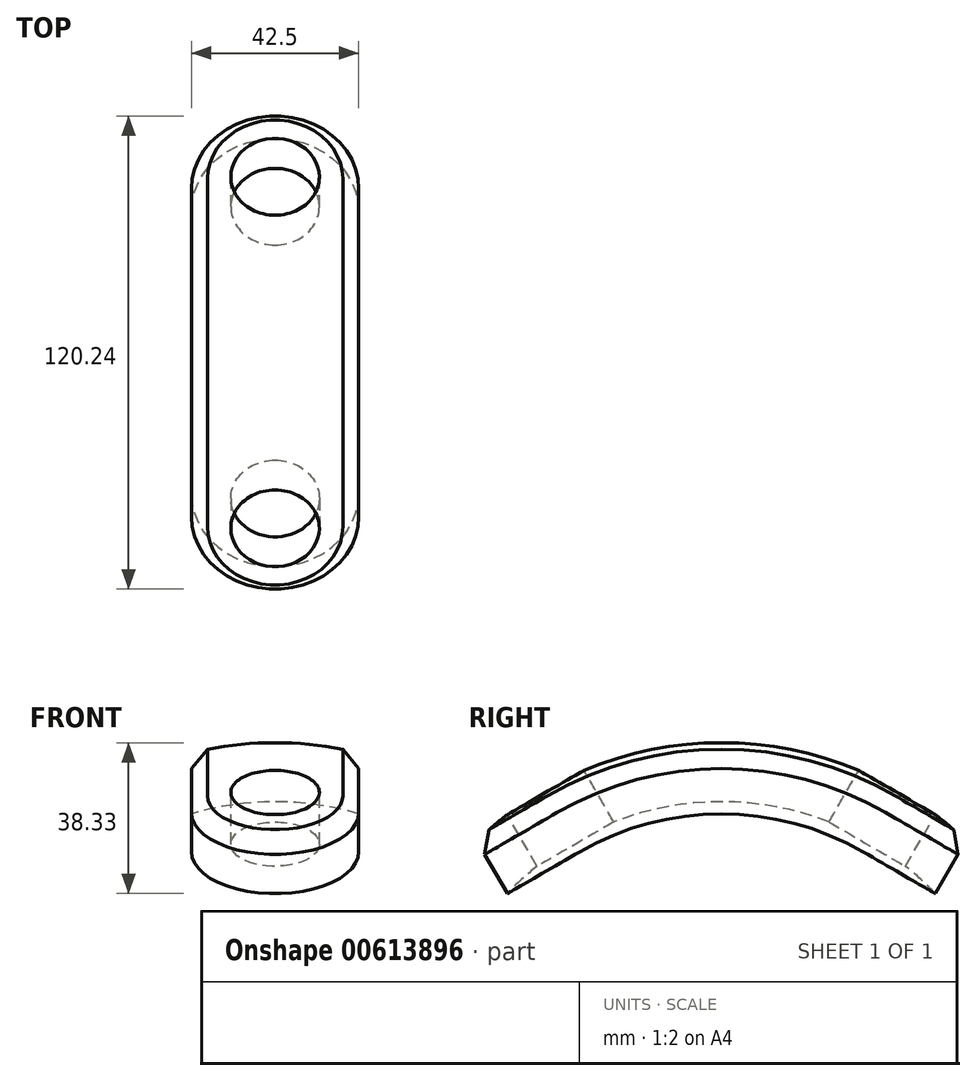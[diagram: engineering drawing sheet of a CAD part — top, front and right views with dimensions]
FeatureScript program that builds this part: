
annotation { "Feature Type Name" : "Feature", "Feature Type Description" : "" }
export const myFeature = defineFeature(function(context is Context, id is Id, definition is map)
    precondition{}
    {
        {
            var Q0;
            Q0=qCreatedBy(makeId("Front.planeOp"),FACE);
            var sketch = newSketch(context, id + "F0", { "sketchPlane" : qUnion([Q0])});
            skArc(sketch, "E0", {"start": v(21.25, 71.93) * mm, "mid": v(0, 75) * mm, "end": v(-21.25, 71.93) * mm});
            skArc(sketch, "E1", {"start": v(21.25, 87.46) * mm, "mid": v(0, 90) * mm, "end": v(-21.25, 87.46) * mm});
            skLineSegment(sketch, "E2", {"start": v(21.25, 71.93) * mm, "end": v(21.25, 87.46) * mm});
            skLineSegment(sketch, "E3.MirrorCS", {"start": v(-21.25, 71.93) * mm, "end": v(-21.25, 87.46) * mm});
            skLineSegment(sketch, "E4", {"start": v(0, 0) * mm, "end": v(12.01, 0) * mm, "construction": true});
            skSolve(sketch);
        }
        {
            var Q0;
            Q0=makeQuery(id+"F0.imprint","IMPRINT",FACE,{"disambiguationData":[TD([[makeQuery(id+"F0.imprint","IMPRINT",EDGE,{"derivedFrom":sQuery(id+"F0.wireOp",EDGE,"E0")}),-1.0]])]});
            var Q1;
            Q1=sQuery(id+"F0.wireOp",EDGE,"E4");
            revolve(context, id + "F1", {"entities" : qUnion([Q0]), "axis" : qUnion([Q1]), "revolveType" : RevolveType.ONE_DIRECTION, "angle" : 30 * degree});
        }
        {
            var Q0;
            Q0=makeQuery(id+"F1.opRevolve","CAP_EDGE",EDGE,{"disambiguationData":[OSD([sQuery(id+"F0.wireOp",EDGE,"E0")])],"isStart":false});
            cPoint(context, id + "F2", {"entities" : qUnion([Q0]), "parameter" : 0.5});
        }
        {
            var Q0;
            Q0=makeQuery(id+"F1.opRevolve","CAP_EDGE",EDGE,{"disambiguationData":[OSD([sQuery(id+"F0.wireOp",EDGE,"E2")])],"isStart":false});
            var Q1;
            Q1 = qCreatedBy(id + "F2" ,VERTEX);
            cPlane(context, id + "F3", {"entities" : qUnion([Q0, Q1]), "cplaneType" : CPlaneType.LINE_POINT, "offset" : 25 * mm, "width" : 150 * mm, "height" : 150 * mm});
        }
        {
            var Q0;
            Q0=qCreatedBy(id+"F3.planeOp",FACE);
            var sketch = newSketch(context, id + "F4", { "sketchPlane" : qUnion([Q0])});
            skCircle(sketch, "E5", {"center": v(0, 0) * mm, "radius": 11.25 * mm});
            skCircle(sketch, "E6", {"center": v(0, 0) * mm, "radius": 21.25 * mm});
            skLineSegment(sketch, "E7", {"start": v(11.25, 0) * mm, "end": v(21.25, 0) * mm});
            skLineSegment(sketch, "E8", {"start": v(-11.25, 0) * mm, "end": v(-21.25, 0) * mm});
            skLineSegment(sketch, "E9", {"start": v(-11.25, 0) * mm, "end": v(11.25, 0) * mm});
            skSolve(sketch);
        }
        {
            var Q0;
            {var subQ0=sQuery(id+"F4.wireOp",EDGE,"E9");Q0=makeQuery(id+"F4.imprint","IMPRINT",FACE,{"disambiguationData":[TD([[makeQuery(id+"F4.imprint","IMPRINT",EDGE,{"derivedFrom":subQ0}),-1.0]])]});}
            var Q1;
            {var subQ0=sQuery(id+"F4.wireOp",EDGE,"E9");Q1=makeQuery(id+"F4.imprint","IMPRINT",FACE,{"disambiguationData":[TD([[makeQuery(id+"F4.imprint","IMPRINT",EDGE,{"derivedFrom":subQ0}),1.0]])]});}
            extrude(context, id + "F5", {"entities" : qUnion([Q0, Q1]), "operationType" : NewBodyOperationType.REMOVE, "endBound" : BoundingType.THROUGH_ALL, "oppositeDirection" : true, "depth" : 25 * mm, "offsetDistance" : 25 * mm, "hasSecondDirection" : true, "secondDirectionBound" : SecondDirectionBoundingType.THROUGH_ALL, "secondDirectionOppositeDirection" : false, "secondDirectionDepth" : 25 * mm});
        }
        {
            var Q0;
            {var subQ0=sQuery(id+"F0.wireOp",EDGE,"E0");var subQ1=sQuery(id+"F0.wireOp",EDGE,"E1");var subQ2=sQuery(id+"F0.wireOp",EDGE,"E2");Q0=makeQuery(id+"F5.boolean.opBoolean","SPLIT",FACE,{"disambiguationData":[TD([makeQuery(id+"F1.opRevolve","SWEPT_FACE",FACE,{"disambiguationData":[OSD([subQ2])]})])],"derivedFrom":makeQuery(id+"F1.opRevolve","CAP_FACE",FACE,{"disambiguationData":[OSD([subQ0,subQ1,subQ2,sQuery(id+"F0.wireOp",EDGE,"E3.MirrorCS")])],"isStart":false})});}
            var Q1;
            Q1=makeQuery(id+"F5.boolean.opBoolean","COPY",FACE,{"derivedFrom":makeQuery(id+"F5.opExtrude","SWEPT_FACE",FACE,{"disambiguationData":[OSD([sQuery(id+"F4.wireOp",EDGE,"E5")])]})});
            revolve(context, id + "F6", {"operationType" : NewBodyOperationType.ADD, "entities" : qUnion([Q0]), "axis" : qUnion([Q1]), "revolveType" : RevolveType.ONE_DIRECTION, "angle" : 180 * degree});
        }
        {
            var Q0;
            Q0=makeQuery(id+"F1.opRevolve","SWEPT_BODY",BODY,{"disambiguationData":[OSD([sQuery(id+"F0.wireOp",EDGE,"E0"),sQuery(id+"F0.wireOp",EDGE,"E1"),sQuery(id+"F0.wireOp",EDGE,"E2"),sQuery(id+"F0.wireOp",EDGE,"E3.MirrorCS")])]});
            var Q1;
            Q1=qCreatedBy(makeId("Front.planeOp"),FACE);
            mirror(context, id + "F7", {"operationType" : NewBodyOperationType.ADD, "entities" : qUnion([Q0]), "mirrorPlane" : qUnion([Q1])});
        }
        {
            var Q0;
            Q0=makeQuery(id+"F6.opRevolve","SWEPT_EDGE",EDGE,{"disambiguationData":[OSD([sQuery(id+"F0.wireOp",EDGE,"E1"),sQuery(id+"F0.wireOp",EDGE,"E2")])]});
            chamfer(context, id + "F8", {"entities" : qUnion([Q0]), "width" : 5 * mm, "tangentPropagation" : true});
        }
    });
